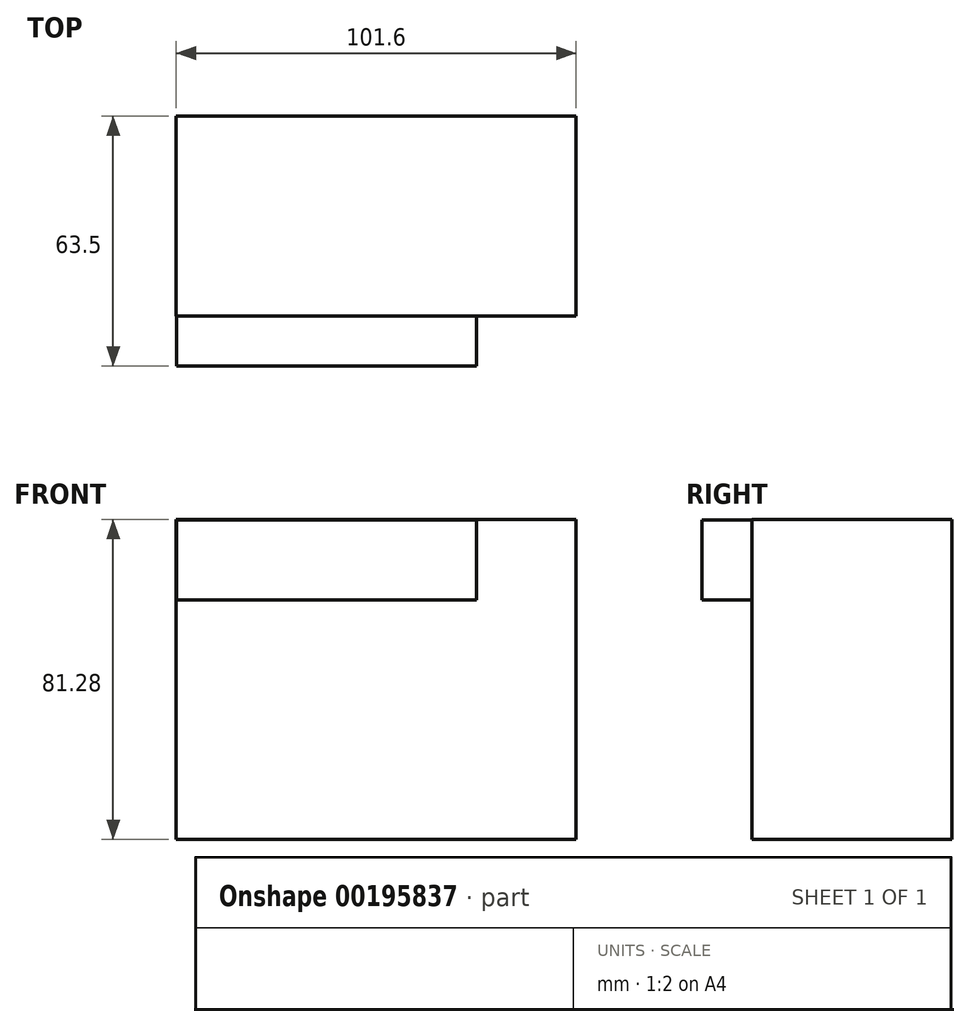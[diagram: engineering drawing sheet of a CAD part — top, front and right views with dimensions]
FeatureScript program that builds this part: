
annotation { "Feature Type Name" : "Feature", "Feature Type Description" : "" }
export const myFeature = defineFeature(function(context is Context, id is Id, definition is map)
    precondition{}
    {
        {
            var Q0;
            Q0=qCreatedBy(makeId("Top.planeOp"),FACE);
            var sketch = newSketch(context, id + "F0", { "sketchPlane" : qUnion([Q0])});
            skLineSegment(sketch, "E0.bottom", {"start": v(-50.8, 25.4) * mm, "end": v(50.8, 25.4) * mm});
            skLineSegment(sketch, "E0.top", {"start": v(-50.8, -25.4) * mm, "end": v(50.8, -25.4) * mm});
            skLineSegment(sketch, "E0.left", {"start": v(-50.8, 25.4) * mm, "end": v(-50.8, -25.4) * mm});
            skLineSegment(sketch, "E0.right", {"start": v(50.8, 25.4) * mm, "end": v(50.8, -25.4) * mm});
            skPoint(sketch, "E0.middle", {"position": v(0, 0) * mm});
            skSolve(sketch);
        }
        {
            var Q0;
            Q0=makeQuery(id+"F0.imprint","IMPRINT",FACE,{"disambiguationData":[TD([[makeQuery(id+"F0.imprint","IMPRINT",EDGE,{"derivedFrom":sQuery(id+"F0.wireOp",EDGE,"E0.bottom")}),-1.0]])]});
            extrude(context, id + "F1", {"entities" : qUnion([Q0]), "depth" : 81.28 * mm});
        }
        {
            var Q0;
            Q0=qCreatedBy(makeId("Front.planeOp"),FACE);
            cPlane(context, id + "F2", {"entities" : qUnion([Q0]), "cplaneType" : CPlaneType.OFFSET, "offset" : 25.4 * mm, "width" : 152.4 * mm, "height" : 152.4 * mm});
        }
        {
            var Q0;
            Q0=qCreatedBy(id+"F2.planeOp",FACE);
            var sketch = newSketch(context, id + "F3", { "sketchPlane" : qUnion([Q0])});
            skLineSegment(sketch, "E1.bottom", {"start": v(-50.71, 81.2) * mm, "end": v(25.49, 81.2) * mm});
            skLineSegment(sketch, "E1.top", {"start": v(-50.71, 60.89) * mm, "end": v(25.49, 60.89) * mm});
            skLineSegment(sketch, "E1.left", {"start": v(-50.71, 81.2) * mm, "end": v(-50.71, 60.89) * mm});
            skLineSegment(sketch, "E1.right", {"start": v(25.49, 81.2) * mm, "end": v(25.49, 60.89) * mm});
            skSolve(sketch);
        }
        {
            var Q0;
            Q0 = qSketchRegion(id + "F3", true);
            extrude(context, id + "F4", {"entities" : qUnion([Q0]), "operationType" : NewBodyOperationType.ADD, "depth" : 12.7 * mm});
        }
    });
